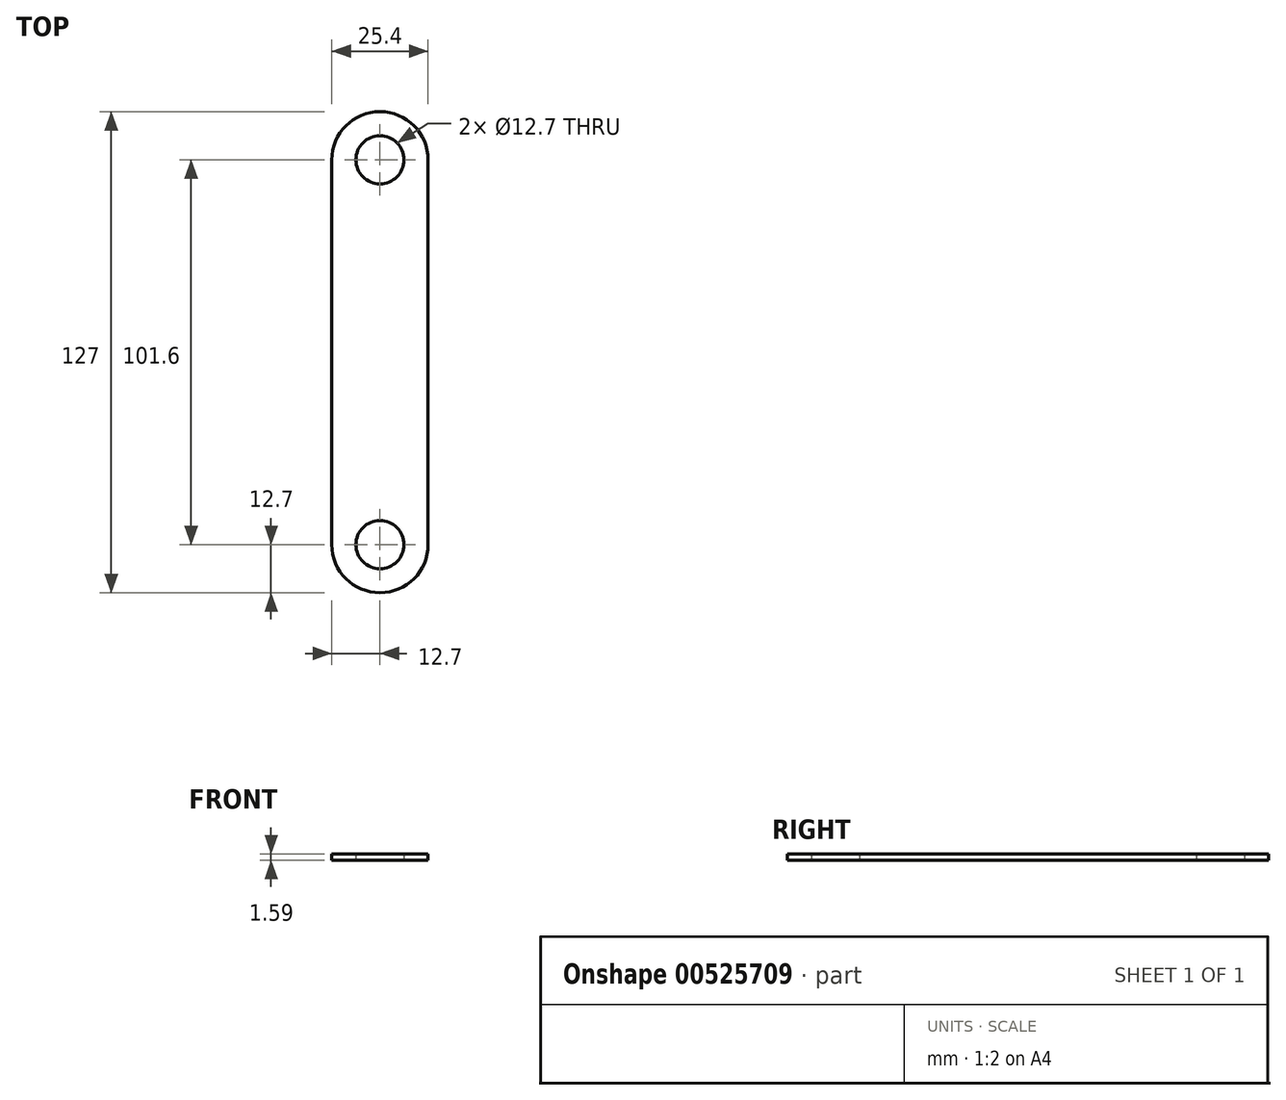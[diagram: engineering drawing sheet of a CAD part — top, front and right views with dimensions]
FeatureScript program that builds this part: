
annotation { "Feature Type Name" : "Feature", "Feature Type Description" : "" }
export const myFeature = defineFeature(function(context is Context, id is Id, definition is map)
    precondition{}
    {
        {
            var Q0;
            Q0=qCreatedBy(makeId("Top.planeOp"),FACE);
            var sketch = newSketch(context, id + "F0", { "sketchPlane" : qUnion([Q0])});
            skLineSegment(sketch, "E0.bottom", {"start": v(-12.7, 50.8) * mm, "end": v(12.7, 50.8) * mm});
            skLineSegment(sketch, "E0.top", {"start": v(-12.7, -50.8) * mm, "end": v(12.7, -50.8) * mm});
            skLineSegment(sketch, "E0.left", {"start": v(-12.7, 50.8) * mm, "end": v(-12.7, -50.8) * mm});
            skLineSegment(sketch, "E0.right", {"start": v(12.7, 50.8) * mm, "end": v(12.7, -50.8) * mm});
            skPoint(sketch, "E0.middle", {"position": v(0, 0) * mm});
            skArc(sketch, "E1", {"start": v(12.7, 50.8) * mm, "mid": v(0, 63.5) * mm, "end": v(-12.7, 50.8) * mm});
            skArc(sketch, "E2", {"start": v(-12.7, -50.8) * mm, "mid": v(0, -63.5) * mm, "end": v(12.7, -50.8) * mm});
            skLineSegment(sketch, "E3", {"start": v(0, 63.5) * mm, "end": v(0, -63.5) * mm});
            skCircle(sketch, "E4", {"center": v(0, 50.8) * mm, "radius": 6.35 * mm});
            skCircle(sketch, "E5", {"center": v(0, -50.8) * mm, "radius": 6.35 * mm});
            skSolve(sketch);
        }
        {
            var Q0;
            Q0 = qSketchRegion(id + "F0", true);
            extrude(context, id + "F1", {"entities" : qUnion([Q0]), "depth" : 1.59 * mm, "offsetDistance" : 25.4 * mm});
        }
    });
